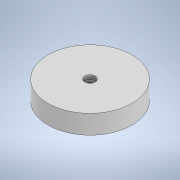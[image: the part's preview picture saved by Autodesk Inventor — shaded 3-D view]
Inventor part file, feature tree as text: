
AUTODESK INVENTOR PART (.ipt)
format: ipt  version: 2020 (Build 240168000, 168)  size: 110,080 bytes
history: native  units: mm
features: sketch x2, extrude x1, hole x1, chamfer x1
ambient origin geometry x8: Origin, YZ Plane, XZ Plane, XY Plane, X Axis, Y Axis, Z Axis, Center Point
bodies: Solid1 (feature_tree)
feature tree (5):
  extrude  "Extrusion1"  Depth=18.0mm TaperAngle=0.0deg
  hole  "Hole1"  [1 undecoded]
  chamfer  "Chamfer1"  [1 undecoded]
  sketch  "Sketch1"  dims[d0=80.0mm d1=18.0mm d2=0.0mm]
  sketch  "Sketch2"  dims[d3=5.2mm d4=6.0mm d5=10.0mm d6=4.0mm d7=90.0deg d8=18.0mm d9=0.0mm d10=3.0mm d11=36.5mm d12=0.349066mm]
note: 2 required parameter values undecoded (feature->parameter linkage not recoverable at this tier; creation-order binding heuristic only, values carry confidence <= 0.55)
